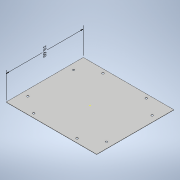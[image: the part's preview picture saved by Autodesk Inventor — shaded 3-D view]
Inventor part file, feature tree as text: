
AUTODESK INVENTOR PART (.ipt)
format: ipt  version: 2021 (Build 250183000, 183)  size: 139,776 bytes
history: native  units: in
note: dims shown in document units (in); Inventor stores cm internally (conversion verified against a paired STEP export)
features: sketch x3, other x2, extrude x2
ambient origin geometry x8: Origin, YZ Plane, XZ Plane, XY Plane, X Axis, Y Axis, Z Axis, Center Point
bodies: Solid1 (feature_tree)
feature tree (7):
  other  "Annotations"
  extrude  "Extrusion1"  Depth=19.6in
  sketch  "Sketch3"  dims[d2=0.06in d3=0.0in d10=4.0in]
  extrude  "Extrusion3"  Depth=0.06in
  sketch  "Sketch1"  dims[d0=23.0in d1=19.6in]
  sketch  "Sketch4"  dims[d11=1.5in d12=0.5in d13=4.0in d14=1.5in d15=0.5in d16=6.0in d18=0.5in d19=6.0in d20=1.5in d21=0.5in d22=4.0in d23=1.5in d24=4.0in d25=1.5in d26=6.0in d27=1.0in d28=0.5in d29=6.0in d30=1.0in d31=0.5in d32=0.5in d33=0.5in d34=1.0in d35=0.0in d39=1.0in d36=0.0in d37=0.3937in d38=19.6in]
  other  "Linear Dimension 1"
